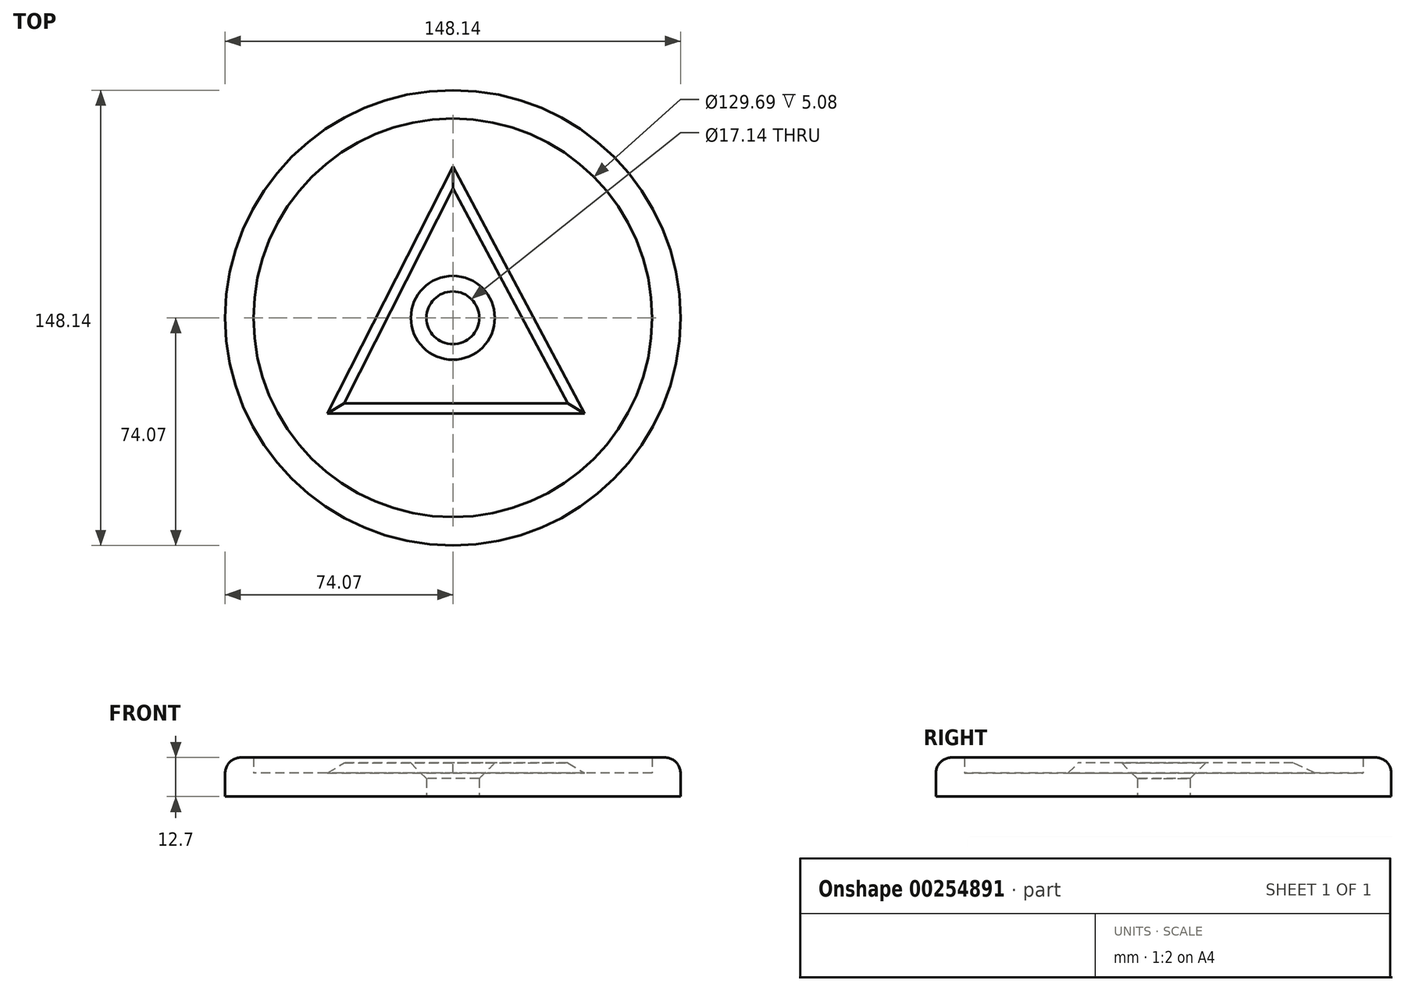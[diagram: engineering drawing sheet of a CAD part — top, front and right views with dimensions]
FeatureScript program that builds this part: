
annotation { "Feature Type Name" : "Feature", "Feature Type Description" : "" }
export const myFeature = defineFeature(function(context is Context, id is Id, definition is map)
    precondition{}
    {
        {
            var Q0;
            Q0=qCreatedBy(makeId("Top.planeOp"),FACE);
            var sketch = newSketch(context, id + "F0", { "sketchPlane" : qUnion([Q0])});
            skLineSegment(sketch, "E0", {"start": v(-43.67, -32.87) * mm, "end": v(45.84, -32.87) * mm});
            skLineSegment(sketch, "E1", {"start": v(45.84, -32.87) * mm, "end": v(0, 53.16) * mm});
            skLineSegment(sketch, "E2", {"start": v(0, 53.16) * mm, "end": v(-43.67, -32.87) * mm});
            skCircle(sketch, "E3", {"center": v(0, 0) * mm, "radius": 74.07 * mm});
            skCircle(sketch, "E4", {"center": v(0, 0) * mm, "radius": 64.85 * mm});
            skCircle(sketch, "E5", {"center": v(0, 0) * mm, "radius": 8.57 * mm});
            skCircle(sketch, "E6", {"center": v(0, 0) * mm, "radius": 4.84 * mm});
            skSolve(sketch);
        }
        {
            var Q0;
            Q0=makeQuery(id+"F0.imprint","IMPRINT",FACE,{"disambiguationData":[TD([[makeQuery(id+"F0.imprint","IMPRINT",EDGE,{"derivedFrom":sQuery(id+"F0.wireOp",EDGE,"E3")}),1.0]])]});
            extrude(context, id + "F1", {"entities" : qUnion([Q0]), "depth" : 12.7 * mm});
        }
        {
            var Q0;
            Q0=makeQuery(id+"F0.imprint","IMPRINT",FACE,{"disambiguationData":[TD([[makeQuery(id+"F0.imprint","IMPRINT",EDGE,{"derivedFrom":sQuery(id+"F0.wireOp",EDGE,"E0")}),-1.0]])]});
            extrude(context, id + "F2", {"entities" : qUnion([Q0]), "operationType" : NewBodyOperationType.ADD, "depth" : 7.62 * mm});
        }
        {
            var Q0;
            Q0=makeQuery(id+"F0.imprint","IMPRINT",FACE,{"disambiguationData":[TD([[makeQuery(id+"F0.imprint","IMPRINT",EDGE,{"derivedFrom":sQuery(id+"F0.wireOp",EDGE,"E0")}),1.0]])]});
            extrude(context, id + "F3", {"entities" : qUnion([Q0]), "operationType" : NewBodyOperationType.ADD, "depth" : 10.92 * mm});
        }
        {
            var Q0;
            Q0=makeQuery(id+"F1.opExtrude","CAP_EDGE",EDGE,{"disambiguationData":[OSD([sQuery(id+"F0.wireOp",EDGE,"E3")])],"isStart":false});
            fillet(context, id + "F4", {"entities" : qUnion([Q0]), "radius" : 5.08 * mm, "tangentPropagation" : true, "allowEdgeOverflow" : false});
        }
        {
            var Q0;
            Q0=makeQuery(id+"F3.opExtrude","CAP_FACE",FACE,{"disambiguationData":[OSD([sQuery(id+"F0.wireOp",EDGE,"E0"),sQuery(id+"F0.wireOp",EDGE,"E1"),sQuery(id+"F0.wireOp",EDGE,"E2"),sQuery(id+"F0.wireOp",EDGE,"E5")])],"isStart":false});
            chamfer(context, id + "F5", {"entities" : qUnion([Q0]), "width" : 5.08 * mm, "tangentPropagation" : true});
        }
    });
